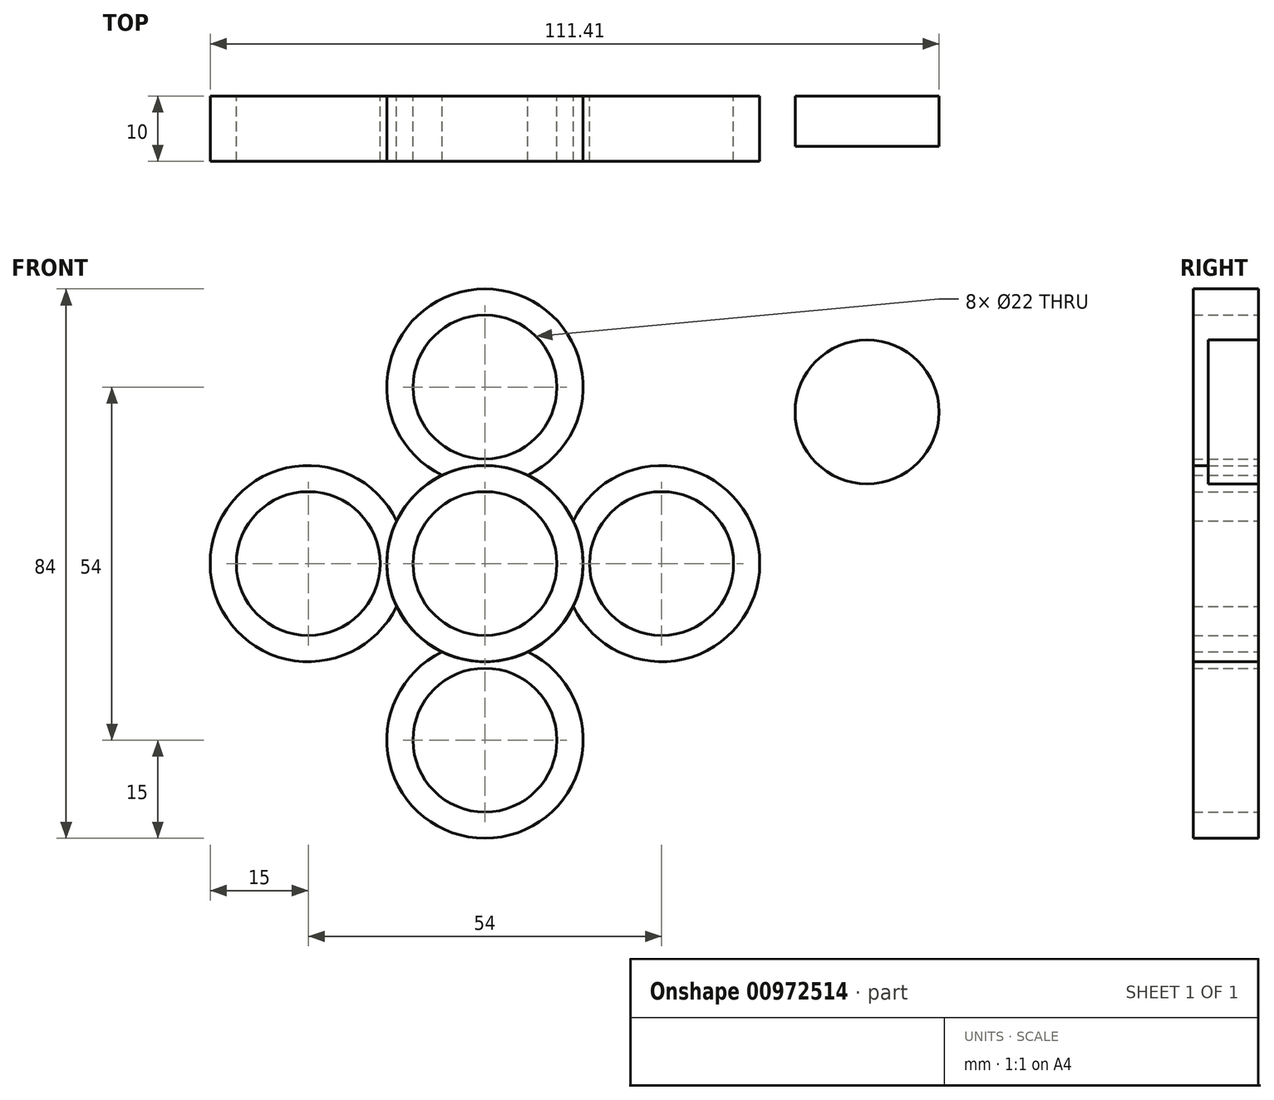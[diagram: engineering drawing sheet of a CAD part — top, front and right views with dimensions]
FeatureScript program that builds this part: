
annotation { "Feature Type Name" : "Feature", "Feature Type Description" : "" }
export const myFeature = defineFeature(function(context is Context, id is Id, definition is map)
    precondition{}
    {
        {
            var Q0;
            Q0=qCreatedBy(makeId("Front.planeOp"),FACE);
            var sketch = newSketch(context, id + "F0", { "sketchPlane" : qUnion([Q0])});
            skCircle(sketch, "E0", {"center": v(0, 0) * mm, "radius": 11 * mm});
            skArc(sketch, "E1", {"start": v(-6.54, 13.5) * mm, "mid": v(0, -15) * mm, "end": v(6.54, 13.5) * mm});
            skCircle(sketch, "E2", {"center": v(0, 27) * mm, "radius": 11 * mm});
            skArc(sketch, "E3", {"start": v(6.54, 13.5) * mm, "mid": v(0, 42) * mm, "end": v(-6.54, 13.5) * mm});
            skSolve(sketch);
        }
        {
            var Q0;
            Q0=makeQuery(id+"F0.imprint","IMPRINT",FACE,{"disambiguationData":[TD([[makeQuery(id+"F0.imprint","IMPRINT",EDGE,{"derivedFrom":sQuery(id+"F0.wireOp",EDGE,"E0")}),-1.0]])]});
            extrude(context, id + "F1", {"entities" : qUnion([Q0]), "depth" : 10 * mm, "offsetDistance" : 25 * mm});
        }
        {
            var Q0;
            Q0=makeQuery(id+"F1.opExtrude","SWEPT_BODY",BODY,{"disambiguationData":[OSD([sQuery(id+"F0.wireOp",EDGE,"E0"),sQuery(id+"F0.wireOp",EDGE,"E1"),sQuery(id+"F0.wireOp",EDGE,"E2"),sQuery(id+"F0.wireOp",EDGE,"E3")])]});
            var Q1;
            Q1=makeQuery(id+"F1.opExtrude","CAP_EDGE",EDGE,{"disambiguationData":[OSD([sQuery(id+"F0.wireOp",EDGE,"E0")])],"isStart":false});
            circularPattern(context, id + "F2", {"entities" : qUnion([Q0]), "axis" : qUnion([Q1]), "angle" : 360 * degree, "instanceCount" : 4, "equalSpace" : true});
        }
        {
            var Q0;
            Q0=qCreatedBy(makeId("Front.planeOp"),FACE);
            var sketch = newSketch(context, id + "F3", { "sketchPlane" : qUnion([Q0])});
            skCircle(sketch, "E4", {"center": v(58.4, 23.2) * mm, "radius": 11 * mm});
            skSolve(sketch);
        }
        {
            var Q0;
            Q0=makeQuery(id+"F3.imprint","IMPRINT",FACE,{"disambiguationData":[TD([[makeQuery(id+"F3.imprint","IMPRINT",EDGE,{"derivedFrom":sQuery(id+"F3.wireOp",EDGE,"E4")}),1.0]])]});
            extrude(context, id + "F4", {"entities" : qUnion([Q0]), "depth" : 7.7 * mm, "offsetDistance" : 25 * mm});
        }
    });
